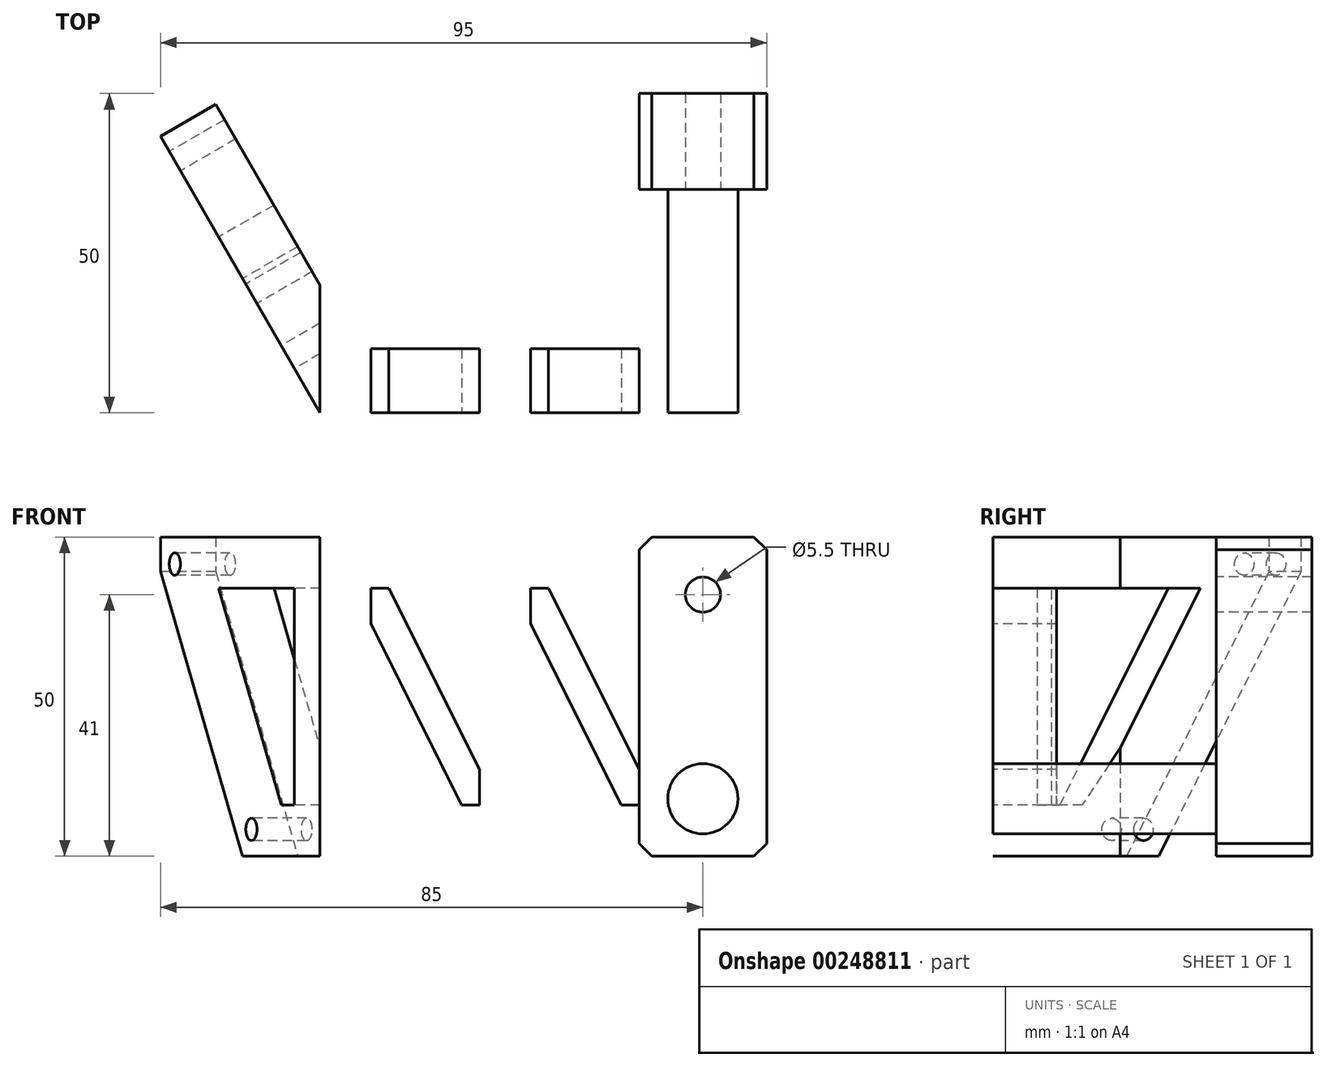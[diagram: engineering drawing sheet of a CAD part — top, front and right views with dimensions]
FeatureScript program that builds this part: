
annotation { "Feature Type Name" : "Feature", "Feature Type Description" : "" }
export const myFeature = defineFeature(function(context is Context, id is Id, definition is map)
    precondition{}
    {
        {
            var Q0;
            Q0=qCreatedBy(makeId("Top.planeOp"),FACE);
            var sketch = newSketch(context, id + "F0", { "sketchPlane" : qUnion([Q0])});
            skLineSegment(sketch, "E0", {"start": v(-54.23, 0) * mm, "end": v(-76.34, 38.3) * mm});
            skLineSegment(sketch, "E1", {"start": v(-76.34, 38.3) * mm, "end": v(-85, 33.3) * mm});
            skLineSegment(sketch, "E2", {"start": v(-85, 33.3) * mm, "end": v(-60, -10) * mm});
            skLineSegment(sketch, "E3", {"start": v(-60, -10) * mm, "end": v(10, -10) * mm});
            skLineSegment(sketch, "E4", {"start": v(10, -10) * mm, "end": v(10, 40) * mm});
            skLineSegment(sketch, "E5", {"start": v(10, 40) * mm, "end": v(-10, 40) * mm});
            skLineSegment(sketch, "E6", {"start": v(-10, 40) * mm, "end": v(-10, 0) * mm});
            skLineSegment(sketch, "E7", {"start": v(-10, 0) * mm, "end": v(-54.23, 0) * mm});
            skSolve(sketch);
        }
        {
            var Q0;
            Q0=makeQuery(id+"F0.imprint","IMPRINT",FACE,{"disambiguationData":[TD([[makeQuery(id+"F0.imprint","IMPRINT",EDGE,{"derivedFrom":sQuery(id+"F0.wireOp",EDGE,"E0")}),1.0]])]});
            extrude(context, id + "F1", {"entities" : qUnion([Q0]), "depth" : 50 * mm, "symmetric" : true});
        }
        {
            var Q0;
            Q0=makeQuery(id+"F1.opExtrude","SWEPT_FACE",FACE,{"disambiguationData":[OSD([sQuery(id+"F0.wireOp",EDGE,"E3")])]});
            var sketch = newSketch(context, id + "F2", { "sketchPlane" : qUnion([Q0])});
            skCircle(sketch, "E8", {"center": v(0, 16) * mm, "radius": 5.5 * mm});
            skCircle(sketch, "E9", {"center": v(0, 16) * mm, "radius": 2.75 * mm});
            skCircle(sketch, "E10.MirrorC", {"center": v(0, -16) * mm, "radius": 5.5 * mm});
            skCircle(sketch, "E11.MirrorC", {"center": v(0, -16) * mm, "radius": 2.75 * mm});
            skLineSegment(sketch, "E12.bottom", {"start": v(-10, 17) * mm, "end": v(-27, 17) * mm});
            skLineSegment(sketch, "E12.top", {"start": v(-10, -17) * mm, "end": v(-27, -17) * mm});
            skLineSegment(sketch, "E12.left", {"start": v(-10, 17) * mm, "end": v(-10, -17) * mm});
            skLineSegment(sketch, "E12.right", {"start": v(-27, 17) * mm, "end": v(-27, -17) * mm});
            skPoint(sketch, "E12.middle", {"position": v(-18.5, 0) * mm});
            skLineSegment(sketch, "E13", {"start": v(-27, 17) * mm, "end": v(-10, -17) * mm});
            skLineSegment(sketch, "E14", {"start": v(-24.2, 17) * mm, "end": v(-10, -11.4) * mm});
            skLineSegment(sketch, "E15", {"start": v(-12.8, -17) * mm, "end": v(-27, 11.4) * mm});
            skLineSegment(sketch, "E16.1.0.0", {"start": v(-35, -17) * mm, "end": v(-52, -17) * mm});
            skLineSegment(sketch, "E16.1.0.1", {"start": v(-52, 17) * mm, "end": v(-35, -17) * mm});
            skLineSegment(sketch, "E16.1.0.2", {"start": v(-35, 17) * mm, "end": v(-52, 17) * mm});
            skLineSegment(sketch, "E16.1.0.3", {"start": v(-49.2, 17) * mm, "end": v(-35, -11.4) * mm});
            skLineSegment(sketch, "E16.1.0.4", {"start": v(-37.8, -17) * mm, "end": v(-52, 11.4) * mm});
            skPoint(sketch, "E16.1.0.5", {"position": v(-43.5, 0) * mm});
            skLineSegment(sketch, "E16.1.0.6", {"start": v(-52, 17) * mm, "end": v(-52, -17) * mm});
            skLineSegment(sketch, "E16.1.0.7", {"start": v(-35, 17) * mm, "end": v(-35, -17) * mm});
            skLineSegment(sketch, "E16.direction1", {"start": v(-27, -17) * mm, "end": v(-52, -17) * mm, "construction": true});
            skSolve(sketch);
        }
        {
            var Q0;
            {var subQ3=sQuery(id+"F2.wireOp",EDGE,"E16.1.0.4");Q0=makeQuery(id+"F2.imprint","IMPRINT",FACE,{"disambiguationData":[TD([[makeQuery(id+"F2.imprint","IMPRINT",EDGE,{"derivedFrom":subQ3}),1.0]])]});}
            var Q1;
            {var subQ3=sQuery(id+"F2.wireOp",EDGE,"E16.1.0.3");Q1=makeQuery(id+"F2.imprint","IMPRINT",FACE,{"disambiguationData":[TD([[makeQuery(id+"F2.imprint","IMPRINT",EDGE,{"derivedFrom":subQ3}),1.0]])]});}
            var Q2;
            {var subQ3=sQuery(id+"F2.wireOp",EDGE,"E14");Q2=makeQuery(id+"F2.imprint","IMPRINT",FACE,{"disambiguationData":[TD([[makeQuery(id+"F2.imprint","IMPRINT",EDGE,{"derivedFrom":subQ3}),1.0]])]});}
            var Q3;
            {var subQ3=sQuery(id+"F2.wireOp",EDGE,"E15");Q3=makeQuery(id+"F2.imprint","IMPRINT",FACE,{"disambiguationData":[TD([[makeQuery(id+"F2.imprint","IMPRINT",EDGE,{"derivedFrom":subQ3}),1.0]])]});}
            var Q4;
            Q4=makeQuery(id+"F2.imprint","IMPRINT",FACE,{"disambiguationData":[TD([[makeQuery(id+"F2.imprint","IMPRINT",EDGE,{"derivedFrom":sQuery(id+"F2.wireOp",EDGE,"E8")}),1.0]])]});
            var Q5;
            Q5=makeQuery(id+"F2.imprint","IMPRINT",FACE,{"disambiguationData":[TD([[makeQuery(id+"F2.imprint","IMPRINT",EDGE,{"derivedFrom":sQuery(id+"F2.wireOp",EDGE,"E10.MirrorC")}),-1.0]])]});
            extrude(context, id + "F3", {"entities" : qUnion([Q0, Q1, Q2, Q3, Q4, Q5]), "operationType" : NewBodyOperationType.REMOVE, "oppositeDirection" : true, "depth" : 35 * mm});
        }
        {
            var Q0;
            Q0=makeQuery(id+"F3.boolean.opBoolean","SPLIT",FACE,{"disambiguationData":[TD([makeQuery(id+"F3.opExtrude","SWEPT_FACE",FACE,{"disambiguationData":[OSD([sQuery(id+"F2.wireOp",EDGE,"E9")])]})])],"derivedFrom":makeQuery(id+"F1.opExtrude","SWEPT_FACE",FACE,{"disambiguationData":[OSD([sQuery(id+"F0.wireOp",EDGE,"E3")])]})});
            var Q1;
            Q1=makeQuery(id+"F3.boolean.opBoolean","SPLIT",FACE,{"disambiguationData":[TD([makeQuery(id+"F3.opExtrude","SWEPT_FACE",FACE,{"disambiguationData":[OSD([sQuery(id+"F2.wireOp",EDGE,"E11.MirrorC")])]})])],"derivedFrom":makeQuery(id+"F1.opExtrude","SWEPT_FACE",FACE,{"disambiguationData":[OSD([sQuery(id+"F0.wireOp",EDGE,"E3")])]})});
            extrude(context, id + "F4", {"entities" : qUnion([Q0, Q1]), "operationType" : NewBodyOperationType.REMOVE, "endBound" : BoundingType.UP_TO_NEXT, "oppositeDirection" : true, "depth" : 25 * mm});
        }
        {
            var Q0;
            Q0=makeQuery(id+"F1.opExtrude","SWEPT_FACE",FACE,{"disambiguationData":[OSD([sQuery(id+"F0.wireOp",EDGE,"E2")])]});
            var sketch = newSketch(context, id + "F5", { "sketchPlane" : qUnion([Q0])});
            skLineSegment(sketch, "E17", {"start": v(-59.17, -2.5) * mm, "end": v(-50.5, 2.5) * mm});
            skPoint(sketch, "E18", {"position": v(-54.84, 0) * mm});
            skLineSegment(sketch, "E19", {"start": v(-54.84, 0) * mm, "end": v(-66.84, 20.78) * mm});
            skLineSegment(sketch, "E20", {"start": v(-54.84, 0) * mm, "end": v(-42.84, -20.78) * mm});
            skCircle(sketch, "E21", {"center": v(-66.84, 20.78) * mm, "radius": 1.75 * mm});
            skCircle(sketch, "E22", {"center": v(-42.84, -20.78) * mm, "radius": 1.75 * mm});
            skLineSegment(sketch, "E23", {"start": v(-45.6, -25) * mm, "end": v(-71.34, 19.58) * mm});
            skLineSegment(sketch, "E24", {"start": v(-29.34, -24.17) * mm, "end": v(-53.1, 17) * mm});
            skLineSegment(sketch, "E25", {"start": v(-53.1, 17) * mm, "end": v(-29.34, 17) * mm});
            skLineSegment(sketch, "E26", {"start": v(-29.34, 17) * mm, "end": v(-29.34, -24.17) * mm});
            skLineSegment(sketch, "E27", {"start": v(-29.34, -17) * mm, "end": v(-33.48, -17) * mm});
            skSolve(sketch);
        }
        {
            var Q0;
            {var subQ0=sQuery(id+"F5.wireOp",EDGE,"E23");var subQ4=makeQuery(id+"F5.imprint","IMPRINT",VERTEX,{"derivedFrom":subQ0});Q0=makeQuery(id+"F5.imprint","IMPRINT",FACE,{"disambiguationData":[TD([[makeQuery(id+"F5.imprint","IMPRINT",EDGE,{"disambiguationData":[TD([[subQ4,1.0]])],"derivedFrom":subQ0}),1.0]])]});}
            var Q1;
            Q1=makeQuery(id+"F5.imprint","IMPRINT",FACE,{"disambiguationData":[TD([[makeQuery(id+"F5.imprint","IMPRINT",EDGE,{"derivedFrom":sQuery(id+"F5.wireOp",EDGE,"E21")}),1.0]])]});
            var Q2;
            {var subQ0=sQuery(id+"F5.wireOp",EDGE,"E25");Q2=makeQuery(id+"F5.imprint","IMPRINT",FACE,{"disambiguationData":[TD([[makeQuery(id+"F5.imprint","IMPRINT",EDGE,{"derivedFrom":subQ0}),-1.0]])]});}
            var Q3;
            Q3=makeQuery(id+"F5.imprint","IMPRINT",FACE,{"disambiguationData":[TD([[makeQuery(id+"F5.imprint","IMPRINT",EDGE,{"derivedFrom":sQuery(id+"F5.wireOp",EDGE,"E22")}),1.0]])]});
            extrude(context, id + "F6", {"entities" : qUnion([Q0, Q1, Q2, Q3]), "operationType" : NewBodyOperationType.REMOVE, "endBound" : BoundingType.UP_TO_NEXT, "oppositeDirection" : true, "depth" : 25 * mm});
        }
        {
            var Q0;
            Q0=makeQuery(id+"F1.opExtrude","CAP_EDGE",EDGE,{"disambiguationData":[OSD([sQuery(id+"F0.wireOp",EDGE,"E3")])],"isStart":true});
            var Q1;
            Q1=makeQuery(id+"F1.opExtrude","CAP_EDGE",EDGE,{"disambiguationData":[OSD([sQuery(id+"F0.wireOp",EDGE,"E7")])],"isStart":true});
            var Q2;
            Q2=makeQuery(id+"F1.opExtrude","CAP_EDGE",EDGE,{"disambiguationData":[OSD([sQuery(id+"F0.wireOp",EDGE,"E6")])],"isStart":true});
            var Q3;
            Q3=makeQuery(id+"F1.opExtrude","CAP_EDGE",EDGE,{"disambiguationData":[OSD([sQuery(id+"F0.wireOp",EDGE,"E4")])],"isStart":true});
            var Q4;
            Q4=makeQuery(id+"F1.opExtrude","SWEPT_EDGE",EDGE,{"disambiguationData":[OSD([sQuery(id+"F0.wireOp",EDGE,"E3"),sQuery(id+"F0.wireOp",EDGE,"E4")])]});
            var Q5;
            Q5=makeQuery(id+"F3.boolean.opBoolean","COPY",EDGE,{"derivedFrom":makeQuery(id+"F3.opExtrude","CAP_EDGE",EDGE,{"disambiguationData":[OSD([sQuery(id+"F2.wireOp",EDGE,"E10.MirrorC")])],"isStart":true})});
            var Q6;
            Q6=makeQuery(id+"F3.boolean.opBoolean","COPY",EDGE,{"derivedFrom":makeQuery(id+"F3.opExtrude","CAP_EDGE",EDGE,{"disambiguationData":[OSD([sQuery(id+"F2.wireOp",EDGE,"E8")])],"isStart":true})});
            var Q7;
            Q7=makeQuery(id+"F3.boolean.opBoolean","COPY",EDGE,{"derivedFrom":makeQuery(id+"F3.opExtrude","CAP_EDGE",EDGE,{"disambiguationData":[OSD([sQuery(id+"F2.wireOp",EDGE,"E12.left")])],"isStart":true})});
            var Q8;
            Q8=makeQuery(id+"F3.boolean.opBoolean","COPY",EDGE,{"derivedFrom":makeQuery(id+"F3.opExtrude","CAP_EDGE",EDGE,{"disambiguationData":[OSD([sQuery(id+"F2.wireOp",EDGE,"E12.bottom")])],"isStart":true})});
            var Q9;
            Q9=makeQuery(id+"F3.boolean.opBoolean","COPY",EDGE,{"derivedFrom":makeQuery(id+"F3.opExtrude","CAP_EDGE",EDGE,{"disambiguationData":[OSD([sQuery(id+"F2.wireOp",EDGE,"E14")])],"isStart":true})});
            var Q10;
            Q10=makeQuery(id+"F3.boolean.opBoolean","COPY",EDGE,{"derivedFrom":makeQuery(id+"F3.opExtrude","CAP_EDGE",EDGE,{"disambiguationData":[OSD([sQuery(id+"F2.wireOp",EDGE,"E15")])],"isStart":true})});
            var Q11;
            {var subQ0=sQuery(id+"F0.wireOp",EDGE,"E2");var subQ5=sQuery(id+"F0.wireOp",EDGE,"E3");Q11=makeQuery(id+"F3.boolean.opBoolean","SPLIT",FACE,{"disambiguationData":[TD([makeQuery(id+"F1.opExtrude","SWEPT_FACE",FACE,{"disambiguationData":[OSD([subQ0])]})])],"derivedFrom":makeQuery(id+"F1.opExtrude","SWEPT_FACE",FACE,{"disambiguationData":[OSD([subQ5])]})});}
            var Q12;
            Q12=makeQuery(id+"F6.boolean.opBoolean","COPY",EDGE,{"derivedFrom":makeQuery(id+"F6.opExtrude","CAP_EDGE",EDGE,{"disambiguationData":[OSD([sQuery(id+"F5.wireOp",EDGE,"E25")])],"isStart":true})});
            var Q13;
            Q13=makeQuery(id+"F6.boolean.opBoolean","COPY",EDGE,{"derivedFrom":makeQuery(id+"F6.opExtrude","CAP_EDGE",EDGE,{"disambiguationData":[OSD([sQuery(id+"F5.wireOp",EDGE,"E26")])],"isStart":true})});
            var Q14;
            Q14=makeQuery(id+"F6.boolean.opBoolean","COPY",EDGE,{"derivedFrom":makeQuery(id+"F6.opExtrude","CAP_EDGE",EDGE,{"disambiguationData":[OSD([sQuery(id+"F5.wireOp",EDGE,"E27")])],"isStart":true})});
            var Q15;
            Q15=makeQuery(id+"F6.boolean.opBoolean","COPY",EDGE,{"derivedFrom":makeQuery(id+"F6.opExtrude","CAP_EDGE",EDGE,{"disambiguationData":[OSD([sQuery(id+"F5.wireOp",EDGE,"E24")])],"isStart":true})});
            var Q16;
            Q16=makeQuery(id+"F6.boolean.opBoolean","COPY",EDGE,{"derivedFrom":makeQuery(id+"F6.opExtrude","CAP_EDGE",EDGE,{"disambiguationData":[OSD([sQuery(id+"F5.wireOp",EDGE,"E26")])],"isStart":false})});
            var Q17;
            Q17=makeQuery(id+"F6.boolean.opBoolean","COPY",EDGE,{"derivedFrom":makeQuery(id+"F6.opExtrude","CAP_EDGE",EDGE,{"disambiguationData":[OSD([sQuery(id+"F5.wireOp",EDGE,"E24")])],"isStart":false})});
            var Q18;
            Q18=makeQuery(id+"F6.boolean.opBoolean","COPY",EDGE,{"derivedFrom":makeQuery(id+"F6.opExtrude","CAP_EDGE",EDGE,{"disambiguationData":[OSD([sQuery(id+"F5.wireOp",EDGE,"E27")])],"isStart":false})});
            var Q19;
            Q19=makeQuery(id+"F6.boolean.opBoolean","COPY",EDGE,{"derivedFrom":makeQuery(id+"F6.opExtrude","CAP_EDGE",EDGE,{"disambiguationData":[OSD([sQuery(id+"F5.wireOp",EDGE,"E25")])],"isStart":false})});
            var Q20;
            Q20=makeQuery(id+"F1.opExtrude","CAP_EDGE",EDGE,{"disambiguationData":[OSD([sQuery(id+"F0.wireOp",EDGE,"E7")])],"isStart":false});
            var Q21;
            Q21=makeQuery(id+"F3.boolean.opBoolean","INTERSECT",EDGE,{"derivedFrom":[makeQuery(id+"F1.opExtrude","SWEPT_FACE",FACE,{"disambiguationData":[OSD([sQuery(id+"F0.wireOp",EDGE,"E7")])]}),makeQuery(id+"F3.opExtrude","SWEPT_FACE",FACE,{"disambiguationData":[OSD([sQuery(id+"F2.wireOp",EDGE,"E16.1.0.2")])]})]});
            var Q22;
            Q22=makeQuery(id+"F3.boolean.opBoolean","INTERSECT",EDGE,{"derivedFrom":[makeQuery(id+"F1.opExtrude","SWEPT_FACE",FACE,{"disambiguationData":[OSD([sQuery(id+"F0.wireOp",EDGE,"E7")])]}),makeQuery(id+"F3.opExtrude","SWEPT_FACE",FACE,{"disambiguationData":[OSD([sQuery(id+"F2.wireOp",EDGE,"E16.1.0.3")])]})]});
            var Q23;
            Q23=makeQuery(id+"F3.boolean.opBoolean","INTERSECT",EDGE,{"derivedFrom":[makeQuery(id+"F1.opExtrude","SWEPT_FACE",FACE,{"disambiguationData":[OSD([sQuery(id+"F0.wireOp",EDGE,"E7")])]}),makeQuery(id+"F3.opExtrude","SWEPT_FACE",FACE,{"disambiguationData":[OSD([sQuery(id+"F2.wireOp",EDGE,"E16.1.0.7")])]})]});
            var Q24;
            Q24=makeQuery(id+"F3.boolean.opBoolean","INTERSECT",EDGE,{"derivedFrom":[makeQuery(id+"F1.opExtrude","SWEPT_FACE",FACE,{"disambiguationData":[OSD([sQuery(id+"F0.wireOp",EDGE,"E7")])]}),makeQuery(id+"F3.opExtrude","SWEPT_FACE",FACE,{"disambiguationData":[OSD([sQuery(id+"F2.wireOp",EDGE,"E16.1.0.4")])]})]});
            var Q25;
            Q25=makeQuery(id+"F3.boolean.opBoolean","INTERSECT",EDGE,{"derivedFrom":[makeQuery(id+"F1.opExtrude","SWEPT_FACE",FACE,{"disambiguationData":[OSD([sQuery(id+"F0.wireOp",EDGE,"E7")])]}),makeQuery(id+"F3.opExtrude","SWEPT_FACE",FACE,{"disambiguationData":[OSD([sQuery(id+"F2.wireOp",EDGE,"E16.1.0.0")])]})]});
            var Q26;
            Q26=makeQuery(id+"F3.boolean.opBoolean","INTERSECT",EDGE,{"derivedFrom":[makeQuery(id+"F1.opExtrude","SWEPT_FACE",FACE,{"disambiguationData":[OSD([sQuery(id+"F0.wireOp",EDGE,"E7")])]}),makeQuery(id+"F3.opExtrude","SWEPT_FACE",FACE,{"disambiguationData":[OSD([sQuery(id+"F2.wireOp",EDGE,"E16.1.0.6")])]})]});
            var Q27;
            Q27=makeQuery(id+"F3.boolean.opBoolean","INTERSECT",EDGE,{"derivedFrom":[makeQuery(id+"F1.opExtrude","SWEPT_FACE",FACE,{"disambiguationData":[OSD([sQuery(id+"F0.wireOp",EDGE,"E7")])]}),makeQuery(id+"F3.opExtrude","SWEPT_FACE",FACE,{"disambiguationData":[OSD([sQuery(id+"F2.wireOp",EDGE,"E12.top")])]})]});
            var Q28;
            Q28=makeQuery(id+"F3.boolean.opBoolean","INTERSECT",EDGE,{"derivedFrom":[makeQuery(id+"F1.opExtrude","SWEPT_FACE",FACE,{"disambiguationData":[OSD([sQuery(id+"F0.wireOp",EDGE,"E7")])]}),makeQuery(id+"F3.opExtrude","SWEPT_FACE",FACE,{"disambiguationData":[OSD([sQuery(id+"F2.wireOp",EDGE,"E12.right")])]})]});
            var Q29;
            Q29=makeQuery(id+"F3.boolean.opBoolean","INTERSECT",EDGE,{"derivedFrom":[makeQuery(id+"F1.opExtrude","SWEPT_FACE",FACE,{"disambiguationData":[OSD([sQuery(id+"F0.wireOp",EDGE,"E7")])]}),makeQuery(id+"F3.opExtrude","SWEPT_FACE",FACE,{"disambiguationData":[OSD([sQuery(id+"F2.wireOp",EDGE,"E15")])]})]});
            var Q30;
            Q30=makeQuery(id+"F3.boolean.opBoolean","INTERSECT",EDGE,{"derivedFrom":[makeQuery(id+"F1.opExtrude","SWEPT_FACE",FACE,{"disambiguationData":[OSD([sQuery(id+"F0.wireOp",EDGE,"E7")])]}),makeQuery(id+"F3.opExtrude","SWEPT_FACE",FACE,{"disambiguationData":[OSD([sQuery(id+"F2.wireOp",EDGE,"E14")])]})]});
            var Q31;
            Q31=makeQuery(id+"F3.boolean.opBoolean","INTERSECT",EDGE,{"derivedFrom":[makeQuery(id+"F1.opExtrude","SWEPT_FACE",FACE,{"disambiguationData":[OSD([sQuery(id+"F0.wireOp",EDGE,"E7")])]}),makeQuery(id+"F3.opExtrude","SWEPT_FACE",FACE,{"disambiguationData":[OSD([sQuery(id+"F2.wireOp",EDGE,"E12.bottom")])]})]});
            var Q32;
            Q32=makeQuery(id+"F1.opExtrude","CAP_EDGE",EDGE,{"disambiguationData":[OSD([sQuery(id+"F0.wireOp",EDGE,"E6")])],"isStart":false});
            var Q33;
            Q33=makeQuery(id+"F1.opExtrude","CAP_EDGE",EDGE,{"disambiguationData":[OSD([sQuery(id+"F0.wireOp",EDGE,"E4")])],"isStart":false});
            chamfer(context, id + "F7", {"entities" : qUnion([Q0, Q1, Q2, Q3, Q4, Q5, Q6, Q7, Q8, Q9, Q10, Q11, Q12, Q13, Q14, Q15, Q16, Q17, Q18, Q19, Q20, Q21, Q22, Q23, Q24, Q25, Q26, Q27, Q28, Q29, Q30, Q31, Q32, Q33]), "width" : 2 * mm, "tangentPropagation" : true});
        }
    });
